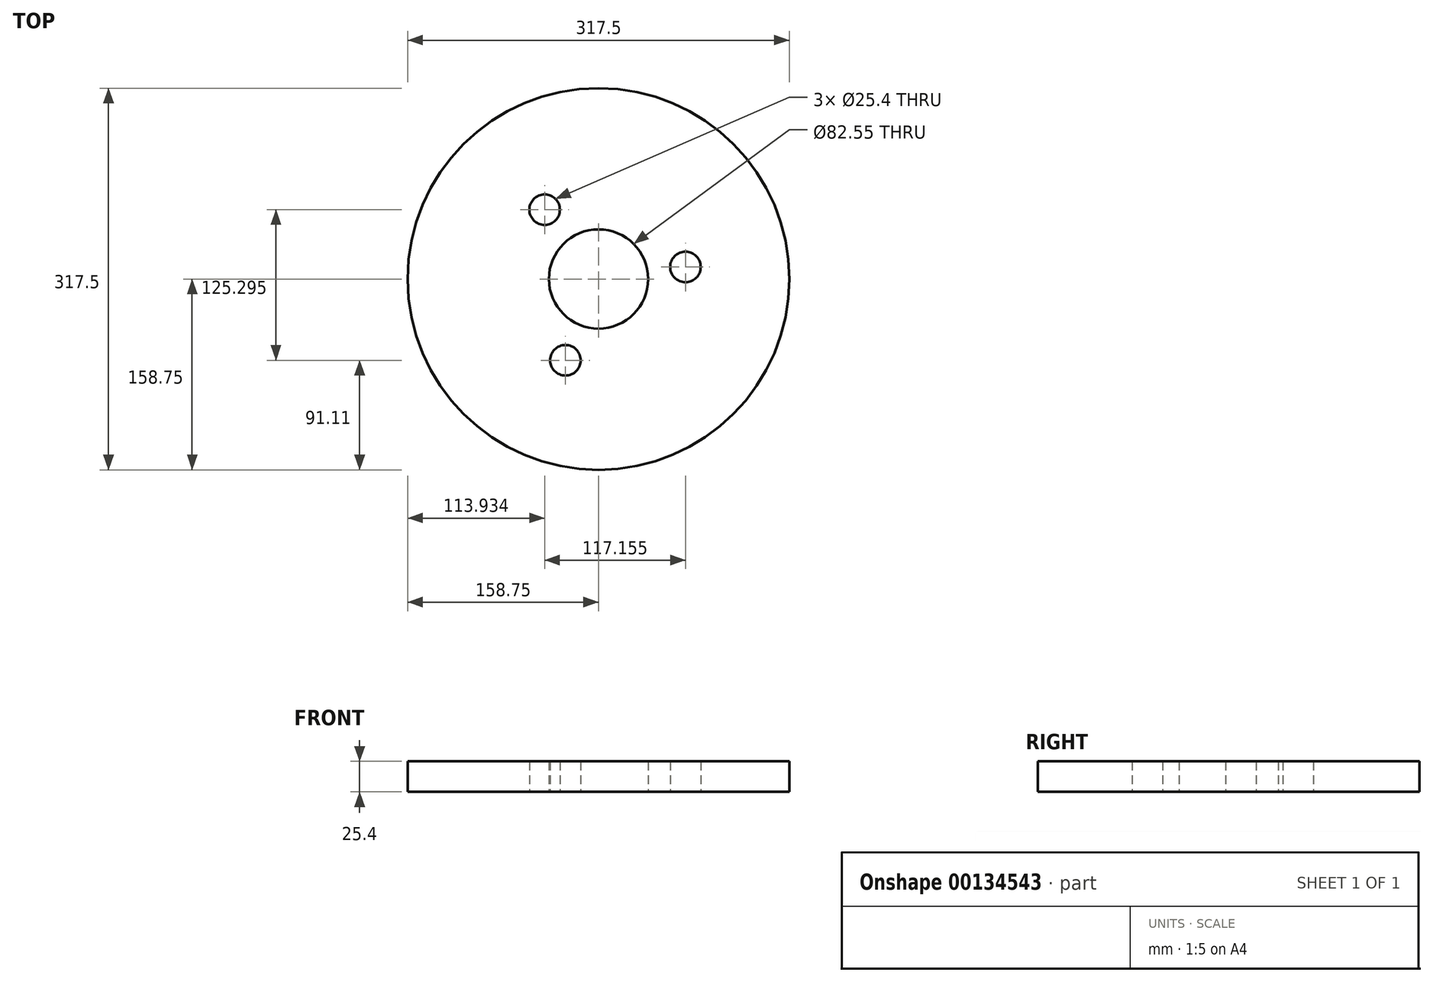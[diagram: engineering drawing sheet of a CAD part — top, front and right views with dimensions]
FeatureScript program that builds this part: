
annotation { "Feature Type Name" : "Feature", "Feature Type Description" : "" }
export const myFeature = defineFeature(function(context is Context, id is Id, definition is map)
    precondition{}
    {
        {
            var Q0;
            Q0=qCreatedBy(makeId("Top.planeOp"),FACE);
            var sketch = newSketch(context, id + "F0", { "sketchPlane" : qUnion([Q0])});
            skCircle(sketch, "E0", {"center": v(0, 0) * mm, "radius": 158.75 * mm});
            skCircle(sketch, "E1", {"center": v(0, 0) * mm, "radius": 41.28 * mm});
            skCircle(sketch, "E2", {"center": v(-44.82, 57.66) * mm, "radius": 12.7 * mm});
            skCircle(sketch, "E3.1.0", {"center": v(-27.52, -67.64) * mm, "radius": 12.7 * mm});
            skCircle(sketch, "E3.2.0", {"center": v(72.34, 9.98) * mm, "radius": 12.7 * mm});
            skSolve(sketch);
        }
        {
            var Q0;
            Q0=makeQuery(id+"F0.imprint","IMPRINT",FACE,{"disambiguationData":[TD([[makeQuery(id+"F0.imprint","IMPRINT",EDGE,{"derivedFrom":sQuery(id+"F0.wireOp",EDGE,"E0")}),1.0]])]});
            extrude(context, id + "F1", {"entities" : qUnion([Q0]), "depth" : 25.4 * mm});
        }
    });
